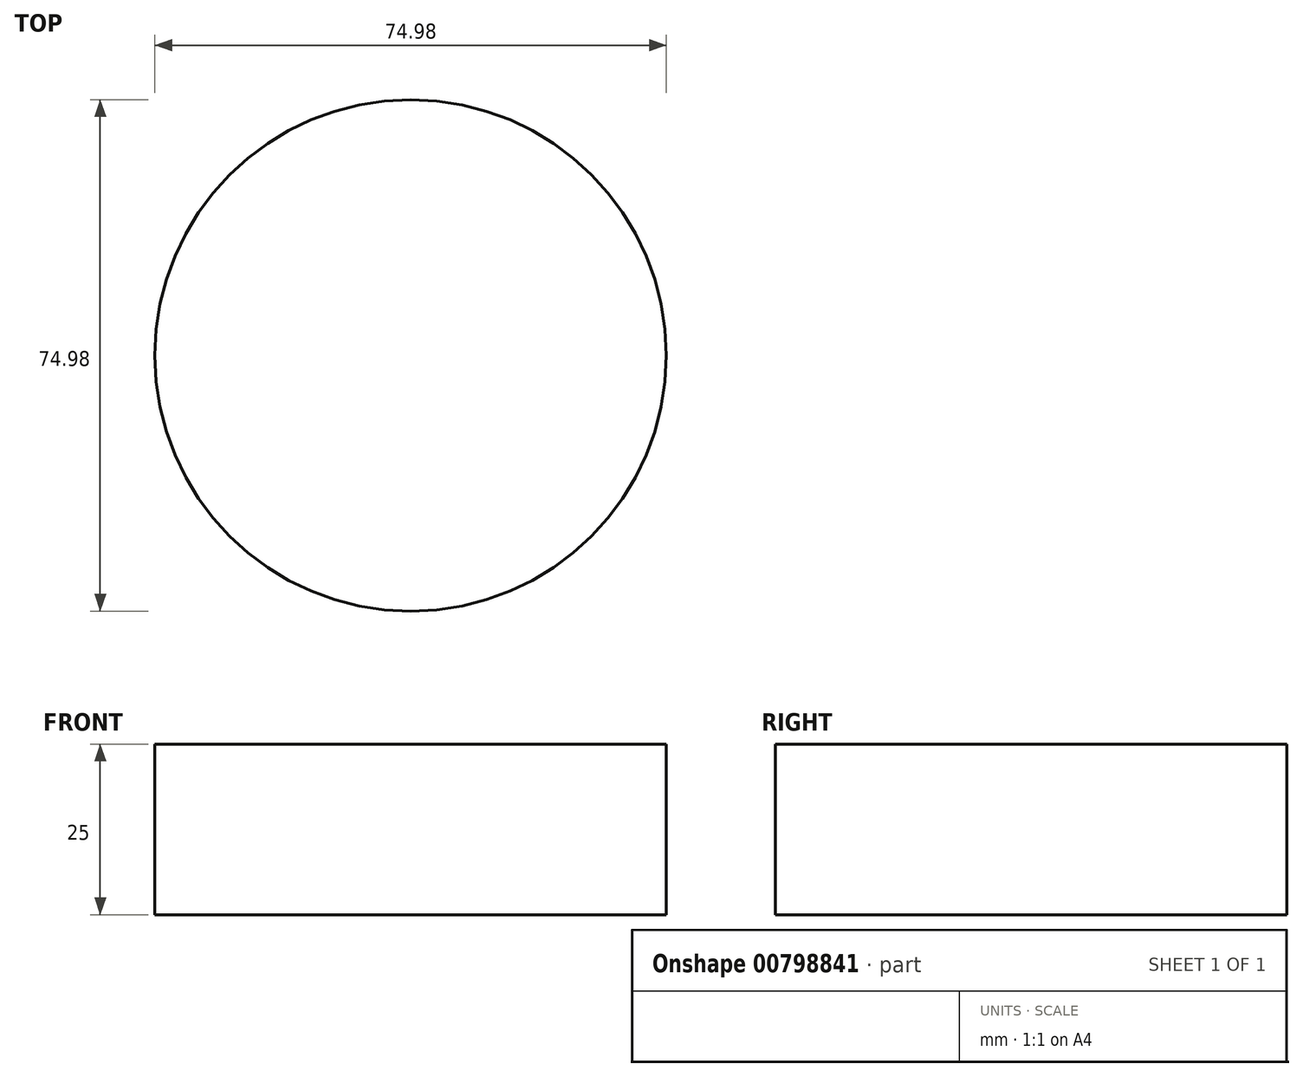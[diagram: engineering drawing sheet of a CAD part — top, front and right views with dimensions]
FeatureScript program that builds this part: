
annotation { "Feature Type Name" : "Feature", "Feature Type Description" : "" }
export const myFeature = defineFeature(function(context is Context, id is Id, definition is map)
    precondition{}
    {
        {
            var Q0;
            Q0=qCreatedBy(makeId("Top.planeOp"),FACE);
            var sketch = newSketch(context, id + "F0", { "sketchPlane" : qUnion([Q0])});
            skCircle(sketch, "E0", {"center": v(0, 0) * mm, "radius": 37.5 * mm});
            skSolve(sketch);
        }
        {
            var Q0;
            Q0 = qSketchRegion(id + "F0", true);
            extrude(context, id + "F1", {"entities" : qUnion([Q0]), "depth" : 25 * mm, "offsetDistance" : 25 * mm});
        }
    });
